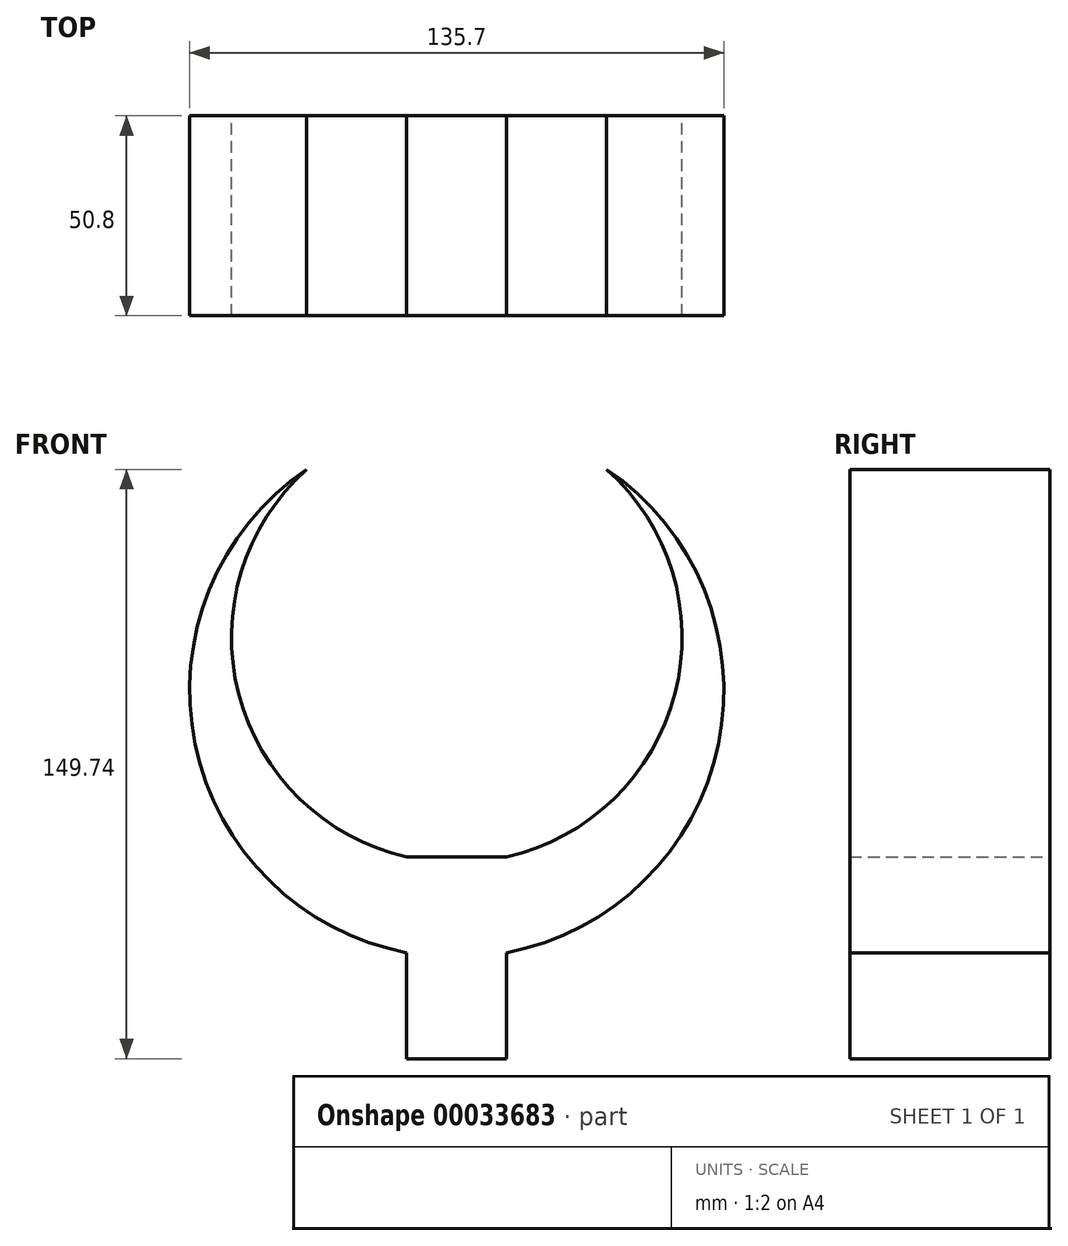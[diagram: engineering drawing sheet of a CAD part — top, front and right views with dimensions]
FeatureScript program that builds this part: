
annotation { "Feature Type Name" : "Feature", "Feature Type Description" : "" }
export const myFeature = defineFeature(function(context is Context, id is Id, definition is map)
    precondition{}
    {
        {
            var Q0;
            Q0=qCreatedBy(makeId("Front.planeOp"),FACE);
            var sketch = newSketch(context, id + "F0", { "sketchPlane" : qUnion([Q0])});
            skLineSegment(sketch, "E0.bottom", {"start": v(-12.7, 0) * mm, "end": v(12.7, 0) * mm});
            skLineSegment(sketch, "E0.top", {"start": v(-12.7, -51.24) * mm, "end": v(12.7, -51.24) * mm});
            skLineSegment(sketch, "E0.left", {"start": v(-12.7, 0) * mm, "end": v(-12.7, -51.24) * mm});
            skLineSegment(sketch, "E0.right", {"start": v(12.7, 0) * mm, "end": v(12.7, -51.24) * mm});
            skArc(sketch, "E1", {"start": v(-38.1, 98.5) * mm, "mid": v(-55.42, 41.51) * mm, "end": v(-12.7, 0) * mm});
            skArc(sketch, "E2", {"start": v(-38.1, 98.5) * mm, "mid": v(0, -25.5) * mm, "end": v(38.1, 98.5) * mm});
            skArc(sketch, "E3", {"start": v(12.7, 0) * mm, "mid": v(55.42, 41.51) * mm, "end": v(38.1, 98.5) * mm});
            skLineSegment(sketch, "E4", {"start": v(0, 167.85) * mm, "end": v(0, 0) * mm});
            skSolve(sketch);
        }
        {
            var Q0;
            Q0 = qSketchRegion(id + "F0", true);
            extrude(context, id + "F1", {"entities" : qUnion([Q0]), "depth" : 50.8 * mm});
        }
    });
